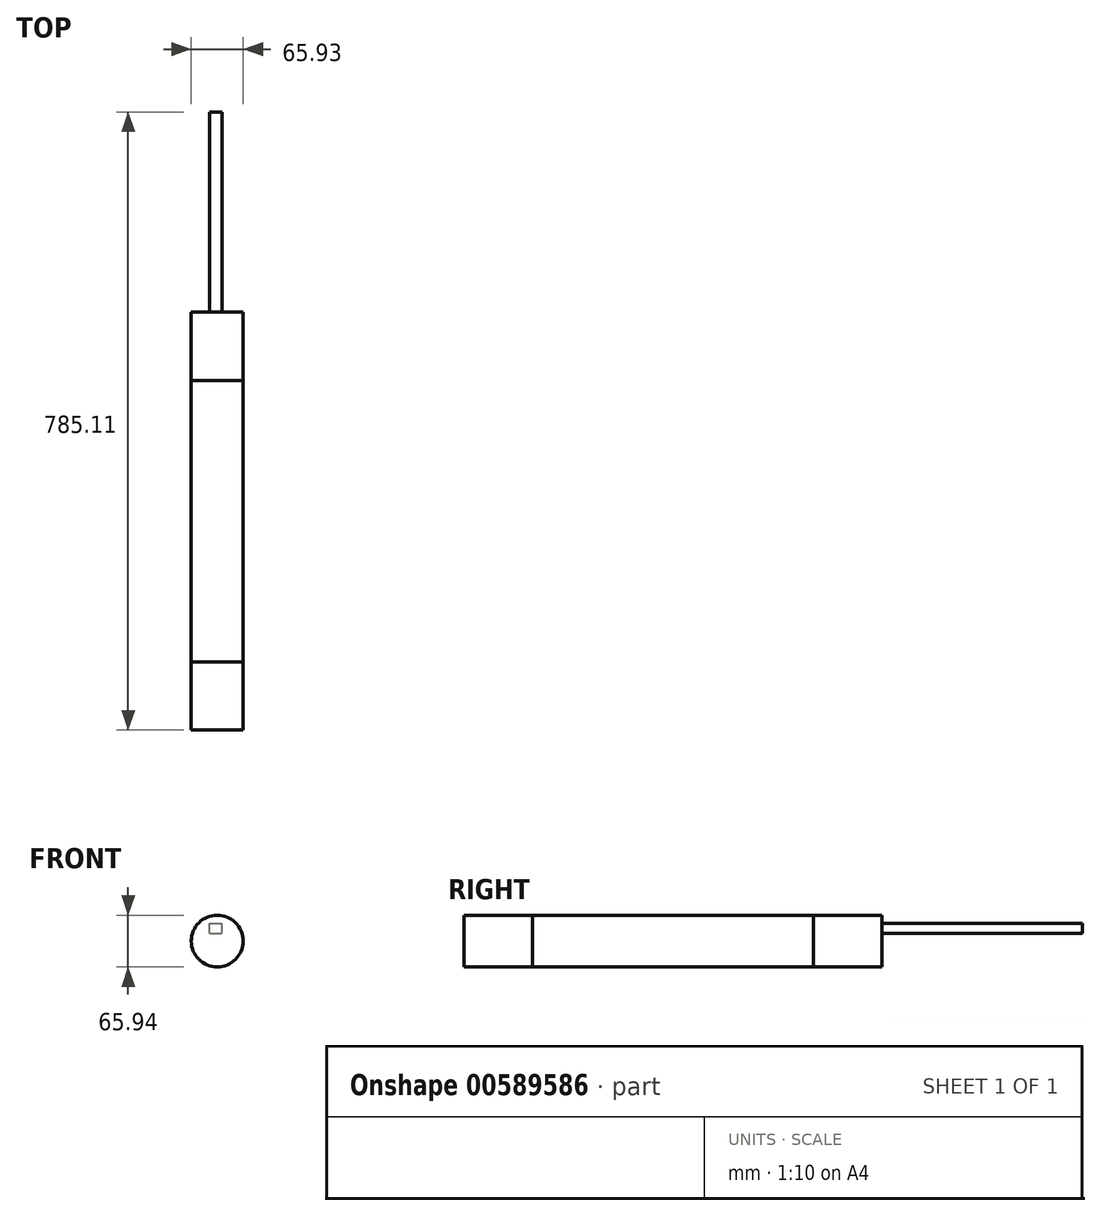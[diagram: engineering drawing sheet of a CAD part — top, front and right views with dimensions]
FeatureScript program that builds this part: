
annotation { "Feature Type Name" : "Feature", "Feature Type Description" : "" }
export const myFeature = defineFeature(function(context is Context, id is Id, definition is map)
    precondition{}
    {
        {
            var Q0;
            Q0=qCreatedBy(makeId("Front.planeOp"),FACE);
            var sketch = newSketch(context, id + "F0", { "sketchPlane" : qUnion([Q0])});
            skCircle(sketch, "E0", {"center": v(33.64, -24.27) * mm, "radius": 32.97 * mm});
            skSolve(sketch);
        }
        {
            var Q0;
            Q0 = qSketchRegion(id + "F0", true);
            extrude(context, id + "F1", {"entities" : qUnion([Q0]), "depth" : 86.87 * mm, "offsetDistance" : 25.4 * mm});
        }
        {
            var Q0;
            Q0=qCreatedBy(makeId("Front.planeOp"),FACE);
            var sketch = newSketch(context, id + "F2", { "sketchPlane" : qUnion([Q0])});
            skLineSegment(sketch, "E1.bottom", {"start": v(23.9, -14.33) * mm, "end": v(39.9, -14.33) * mm});
            skLineSegment(sketch, "E1.top", {"start": v(23.9, -1.88) * mm, "end": v(39.9, -1.88) * mm});
            skLineSegment(sketch, "E1.left", {"start": v(23.9, -14.33) * mm, "end": v(23.9, -1.88) * mm});
            skLineSegment(sketch, "E1.right", {"start": v(39.9, -14.33) * mm, "end": v(39.9, -1.88) * mm});
            skSolve(sketch);
        }
        {
            var Q0;
            Q0 = qSketchRegion(id + "F2", true);
            extrude(context, id + "F3", {"entities" : qUnion([Q0]), "oppositeDirection" : true, "depth" : 254.25 * mm, "offsetDistance" : 25.4 * mm});
        }
        {
            var Q0;
            Q0=makeQuery(id+"F0.imprint","IMPRINT",FACE,{"disambiguationData":[TD([[makeQuery(id+"F0.imprint","IMPRINT",EDGE,{"derivedFrom":sQuery(id+"F0.wireOp",EDGE,"E0")}),1.0]])]});
            var Q1;
            Q1=makeQuery(id+"F1.opExtrude","CAP_FACE",FACE,{"disambiguationData":[OSD([sQuery(id+"F0.wireOp",EDGE,"E0")])],"isStart":true});
            var Q2;
            Q2=makeQuery(id+"F1.opExtrude","CAP_FACE",FACE,{"disambiguationData":[OSD([sQuery(id+"F0.wireOp",EDGE,"E0")])],"isStart":false});
            extrude(context, id + "F4", {"entities" : qUnion([Q0, Q1, Q2]), "depth" : 444 * mm, "offsetDistance" : 25.4 * mm});
        }
    });
